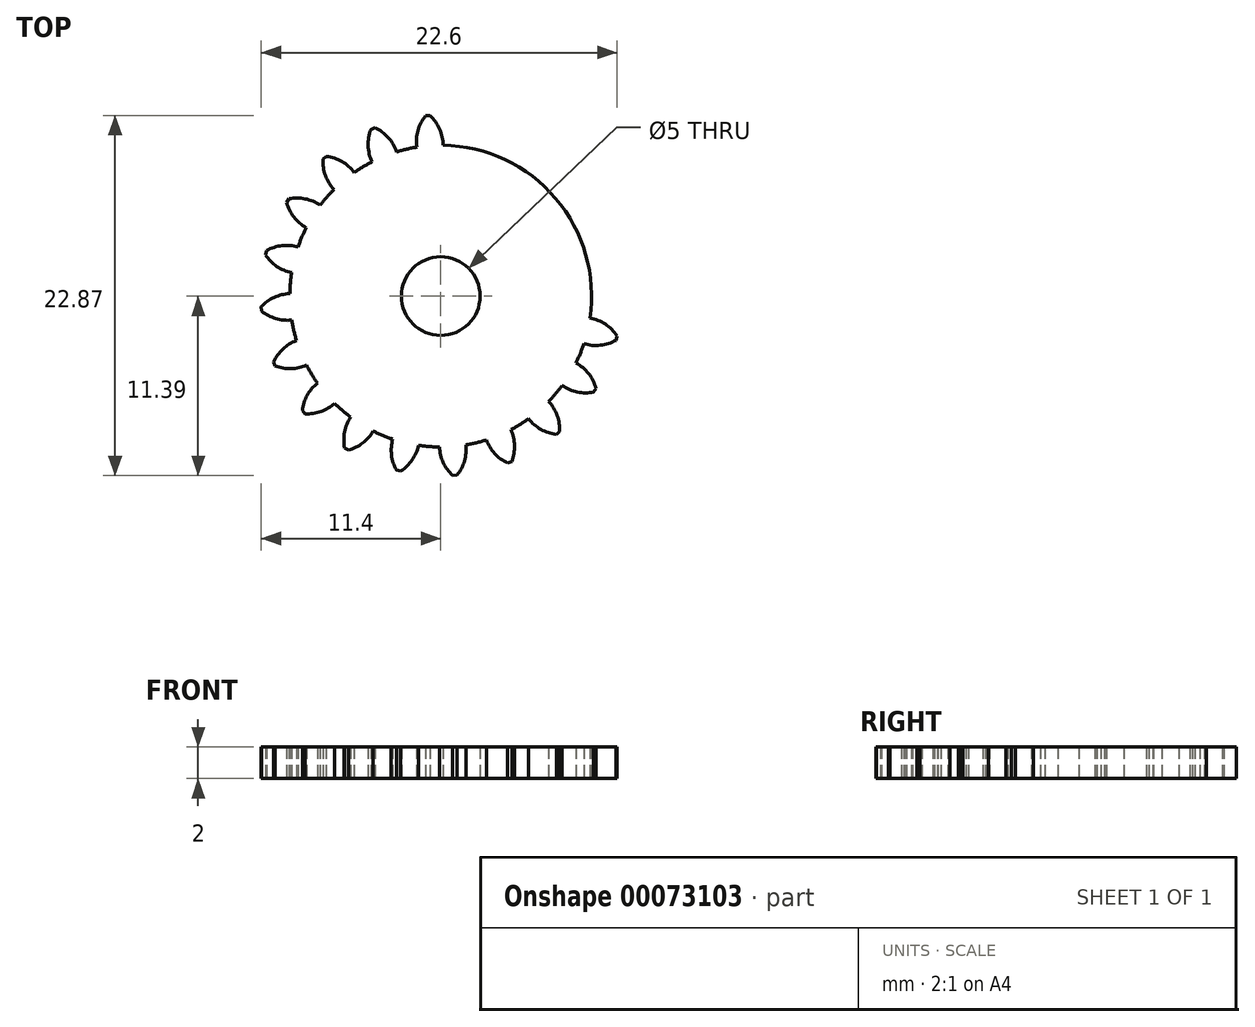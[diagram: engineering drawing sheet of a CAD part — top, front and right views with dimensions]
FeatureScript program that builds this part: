
annotation { "Feature Type Name" : "Feature", "Feature Type Description" : "" }
export const myFeature = defineFeature(function(context is Context, id is Id, definition is map)
    precondition{}
    {
        {
            assignVariable(context, id + "F0", {"name" : "GearDepth", "anyValue" : 2});
        }
        {
            var Q0;
            Q0=qCreatedBy(makeId("Top.planeOp"),FACE);
            var sketch = newSketch(context, id + "F1", { "sketchPlane" : qUnion([Q0])});
            skCircle(sketch, "E0", {"center": v(0, 0) * mm, "radius": 9.58 * mm});
            skCircle(sketch, "E1", {"center": v(0, 0) * mm, "radius": 10.54 * mm, "construction": true});
            skCircle(sketch, "E2", {"center": v(0, 0) * mm, "radius": 11.5 * mm, "construction": true});
            skLineSegment(sketch, "E3", {"start": v(0, 0) * mm, "end": v(0, 17.6) * mm, "construction": true});
            skLineSegment(sketch, "E4", {"start": v(0, 0) * mm, "end": v(-1.29, 18) * mm, "construction": true});
            skLineSegment(sketch, "E5", {"start": v(0, 10.54) * mm, "end": v(-10.54, 10.54) * mm, "construction": true});
            skLineSegment(sketch, "E6", {"start": v(0, 10.54) * mm, "end": v(-10.15, 6.44) * mm, "construction": true});
            skCircle(sketch, "E7", {"center": v(0, 10.54) * mm, "radius": 2.64 * mm, "construction": true});
            skCircle(sketch, "E8", {"center": v(-2.44, 9.55) * mm, "radius": 2.64 * mm, "construction": true});
            skArc(sketch, "E9", {"start": v(-4.89, 10.54) * mm, "mid": v(-4.92, 10.46) * mm, "end": v(-4.95, 10.38) * mm});
            skArc(sketch, "E10.trimOffspring", {"start": v(0.16, 9.58) * mm, "mid": v(-0.07, 10.62) * mm, "end": v(-0.68, 11.48) * mm});
            skArc(sketch, "E11.MirrorCS", {"start": v(-1.52, 9.46) * mm, "mid": v(-1.45, 10.52) * mm, "end": v(-0.96, 11.46) * mm});
            skLineSegment(sketch, "E12", {"start": v(-0.96, 11.46) * mm, "end": v(-0.68, 11.48) * mm});
            skArc(sketch, "E13.1.0", {"start": v(-2.8, 9.15) * mm, "mid": v(-3.33, 10.07) * mm, "end": v(-4.18, 10.7) * mm});
            skLineSegment(sketch, "E13.1.1", {"start": v(-4.44, 10.6) * mm, "end": v(-4.18, 10.7) * mm});
            skArc(sketch, "E13.1.2", {"start": v(-4.35, 8.52) * mm, "mid": v(-4.6, 9.55) * mm, "end": v(-4.44, 10.6) * mm});
            skArc(sketch, "E13.2.0", {"start": v(-5.47, 7.83) * mm, "mid": v(-6.26, 8.54) * mm, "end": v(-7.27, 8.87) * mm});
            skLineSegment(sketch, "E13.2.1", {"start": v(-7.48, 8.7) * mm, "end": v(-7.27, 8.87) * mm});
            skArc(sketch, "E13.2.2", {"start": v(-6.76, 6.75) * mm, "mid": v(-7.32, 7.65) * mm, "end": v(-7.48, 8.7) * mm});
            skArc(sketch, "E13.3.0", {"start": v(-7.6, 5.75) * mm, "mid": v(-8.58, 6.17) * mm, "end": v(-9.64, 6.18) * mm});
            skLineSegment(sketch, "E13.3.1", {"start": v(-9.78, 5.95) * mm, "end": v(-9.64, 6.18) * mm});
            skArc(sketch, "E13.3.2", {"start": v(-8.5, 4.32) * mm, "mid": v(-9.3, 5) * mm, "end": v(-9.78, 5.95) * mm});
            skArc(sketch, "E13.4.0", {"start": v(-9, 3.1) * mm, "mid": v(-10.05, 3.21) * mm, "end": v(-11.06, 2.9) * mm});
            skLineSegment(sketch, "E13.4.1", {"start": v(-11.13, 2.62) * mm, "end": v(-11.06, 2.9) * mm});
            skArc(sketch, "E13.4.2", {"start": v(-9.4, 1.47) * mm, "mid": v(-10.38, 1.87) * mm, "end": v(-11.13, 2.62) * mm});
            skArc(sketch, "E13.5.0", {"start": v(-9.5, 0.16) * mm, "mid": v(-10.53, -0.06) * mm, "end": v(-11.4, -0.68) * mm});
            skLineSegment(sketch, "E13.5.1", {"start": v(-11.38, -0.95) * mm, "end": v(-11.4, -0.68) * mm});
            skArc(sketch, "E13.5.2", {"start": v(-9.38, -1.51) * mm, "mid": v(-10.44, -1.44) * mm, "end": v(-11.38, -0.95) * mm});
            skArc(sketch, "E13.6.0", {"start": v(-9.07, -2.8) * mm, "mid": v(-9.98, -3.32) * mm, "end": v(-10.61, -4.17) * mm});
            skLineSegment(sketch, "E13.6.1", {"start": v(-10.51, -4.43) * mm, "end": v(-10.61, -4.17) * mm});
            skArc(sketch, "E13.6.2", {"start": v(-8.44, -4.35) * mm, "mid": v(-9.46, -4.6) * mm, "end": v(-10.51, -4.43) * mm});
            skArc(sketch, "E13.7.0", {"start": v(-7.75, -5.47) * mm, "mid": v(-8.45, -6.26) * mm, "end": v(-8.79, -7.26) * mm});
            skLineSegment(sketch, "E13.7.1", {"start": v(-8.61, -7.47) * mm, "end": v(-8.79, -7.26) * mm});
            skArc(sketch, "E13.7.2", {"start": v(-6.67, -6.75) * mm, "mid": v(-7.56, -7.31) * mm, "end": v(-8.61, -7.47) * mm});
            skArc(sketch, "E13.8.0", {"start": v(-5.66, -7.6) * mm, "mid": v(-6.1, -8.57) * mm, "end": v(-6.1, -9.63) * mm});
            skLineSegment(sketch, "E13.8.1", {"start": v(-5.86, -9.78) * mm, "end": v(-6.1, -9.63) * mm});
            skArc(sketch, "E13.8.2", {"start": v(-4.24, -8.49) * mm, "mid": v(-4.92, -9.3) * mm, "end": v(-5.86, -9.78) * mm});
            skArc(sketch, "E13.9.0", {"start": v(-3.02, -9) * mm, "mid": v(-3.13, -10.04) * mm, "end": v(-2.81, -11.05) * mm});
            skLineSegment(sketch, "E13.9.1", {"start": v(-2.54, -11.12) * mm, "end": v(-2.81, -11.05) * mm});
            skArc(sketch, "E13.9.2", {"start": v(-1.4, -9.4) * mm, "mid": v(-1.79, -10.38) * mm, "end": v(-2.54, -11.12) * mm});
            skArc(sketch, "E13.10.0", {"start": v(-0.08, -9.5) * mm, "mid": v(0.14, -10.53) * mm, "end": v(0.76, -11.4) * mm});
            skLineSegment(sketch, "E13.10.1", {"start": v(1.04, -11.37) * mm, "end": v(0.76, -11.4) * mm});
            skArc(sketch, "E13.10.2", {"start": v(1.6, -9.37) * mm, "mid": v(1.52, -10.43) * mm, "end": v(1.04, -11.37) * mm});
            skArc(sketch, "E13.11.0", {"start": v(2.87, -9.06) * mm, "mid": v(3.4, -9.98) * mm, "end": v(4.26, -10.6) * mm});
            skLineSegment(sketch, "E13.11.1", {"start": v(4.51, -10.5) * mm, "end": v(4.26, -10.6) * mm});
            skArc(sketch, "E13.11.2", {"start": v(4.43, -8.43) * mm, "mid": v(4.69, -9.46) * mm, "end": v(4.51, -10.5) * mm});
            skArc(sketch, "E13.12.0", {"start": v(5.55, -7.74) * mm, "mid": v(6.34, -8.45) * mm, "end": v(7.34, -8.78) * mm});
            skLineSegment(sketch, "E13.12.1", {"start": v(7.56, -8.6) * mm, "end": v(7.34, -8.78) * mm});
            skArc(sketch, "E13.12.2", {"start": v(6.83, -6.66) * mm, "mid": v(7.4, -7.56) * mm, "end": v(7.56, -8.6) * mm});
            skArc(sketch, "E13.13.0", {"start": v(7.69, -5.66) * mm, "mid": v(8.65, -6.09) * mm, "end": v(9.71, -6.1) * mm});
            skLineSegment(sketch, "E13.13.1", {"start": v(9.86, -5.86) * mm, "end": v(9.71, -6.1) * mm});
            skArc(sketch, "E13.13.2", {"start": v(8.57, -4.23) * mm, "mid": v(9.38, -4.91) * mm, "end": v(9.86, -5.86) * mm});
            skArc(sketch, "E13.14.0", {"start": v(9.07, -3.01) * mm, "mid": v(10.13, -3.12) * mm, "end": v(11.14, -2.8) * mm});
            skLineSegment(sketch, "E13.14.1", {"start": v(11.2, -2.53) * mm, "end": v(11.14, -2.8) * mm});
            skArc(sketch, "E13.14.2", {"start": v(9.48, -1.39) * mm, "mid": v(10.46, -1.78) * mm, "end": v(11.2, -2.53) * mm});
            skArc(sketch, "E13.15.0", {"start": v(9.58, -0.07) * mm, "mid": v(10.61, 0.15) * mm, "end": v(11.47, 0.76) * mm});
            skLineSegment(sketch, "E13.15.1", {"start": v(11.45, 1.04) * mm, "end": v(11.47, 0.76) * mm});
            skArc(sketch, "E13.15.2", {"start": v(9.46, 1.6) * mm, "mid": v(10.51, 1.53) * mm, "end": v(11.45, 1.04) * mm});
            skArc(sketch, "E13.16.0", {"start": v(9.15, 2.88) * mm, "mid": v(10.06, 3.41) * mm, "end": v(10.7, 4.26) * mm});
            skLineSegment(sketch, "E13.16.1", {"start": v(10.59, 4.52) * mm, "end": v(10.7, 4.26) * mm});
            skArc(sketch, "E13.16.2", {"start": v(8.51, 4.44) * mm, "mid": v(9.54, 4.7) * mm, "end": v(10.59, 4.52) * mm});
            skArc(sketch, "E13.17.0", {"start": v(7.82, 5.56) * mm, "mid": v(8.53, 6.34) * mm, "end": v(8.87, 7.35) * mm});
            skLineSegment(sketch, "E13.17.1", {"start": v(8.69, 7.56) * mm, "end": v(8.87, 7.35) * mm});
            skArc(sketch, "E13.17.2", {"start": v(6.74, 6.84) * mm, "mid": v(7.64, 7.4) * mm, "end": v(8.69, 7.56) * mm});
            skArc(sketch, "E13.18.0", {"start": v(5.74, 7.7) * mm, "mid": v(6.17, 8.66) * mm, "end": v(6.18, 9.72) * mm});
            skLineSegment(sketch, "E13.18.1", {"start": v(5.94, 9.87) * mm, "end": v(6.18, 9.72) * mm});
            skArc(sketch, "E13.18.2", {"start": v(4.31, 8.58) * mm, "mid": v(5, 9.4) * mm, "end": v(5.94, 9.87) * mm});
            skArc(sketch, "E13.19.0", {"start": v(3.1, 9.08) * mm, "mid": v(3.2, 10.13) * mm, "end": v(2.89, 11.14) * mm});
            skLineSegment(sketch, "E13.19.1", {"start": v(2.62, 11.2) * mm, "end": v(2.89, 11.14) * mm});
            skArc(sketch, "E13.19.2", {"start": v(1.47, 9.48) * mm, "mid": v(1.86, 10.46) * mm, "end": v(2.62, 11.2) * mm});
            skPoint(sketch, "E13.center", {"position": v(0.04, 0.04) * mm});
            skCircle(sketch, "E14", {"center": v(0, 0) * mm, "radius": 2.5 * mm});
            skSolve(sketch);
        }
        {
            var Q0;
            {var subQ0=sQuery(id+"F1.wireOp",EDGE,"E10.trimOffspring");Q0=makeQuery(id+"F1.imprint","IMPRINT",FACE,{"disambiguationData":[TD([[makeQuery(id+"F1.imprint","IMPRINT",EDGE,{"derivedFrom":subQ0}),1.0]])]});}
            var Q1;
            {var subQ0=sQuery(id+"F1.wireOp",EDGE,"E0");var subQ1=makeQuery(id+"F1.imprint","INTERSECT",VERTEX,{"derivedFrom":[subQ0,sQuery(id+"F1.wireOp",EDGE,"E10.trimOffspring")]});Q1=makeQuery(id+"F1.imprint","IMPRINT",FACE,{"disambiguationData":[TD([[makeQuery(id+"F1.imprint","IMPRINT",EDGE,{"disambiguationData":[TD([[subQ1,-1.0]])],"derivedFrom":subQ0}),1.0]])]});}
            var Q2;
            {var subQ0=sQuery(id+"F1.wireOp",EDGE,"E13.1.0");Q2=makeQuery(id+"F1.imprint","IMPRINT",FACE,{"disambiguationData":[TD([[makeQuery(id+"F1.imprint","IMPRINT",EDGE,{"derivedFrom":subQ0}),1.0]])]});}
            var Q3;
            {var subQ0=sQuery(id+"F1.wireOp",EDGE,"E13.2.0");Q3=makeQuery(id+"F1.imprint","IMPRINT",FACE,{"disambiguationData":[TD([[makeQuery(id+"F1.imprint","IMPRINT",EDGE,{"derivedFrom":subQ0}),1.0]])]});}
            var Q4;
            {var subQ0=sQuery(id+"F1.wireOp",EDGE,"E13.3.0");Q4=makeQuery(id+"F1.imprint","IMPRINT",FACE,{"disambiguationData":[TD([[makeQuery(id+"F1.imprint","IMPRINT",EDGE,{"derivedFrom":subQ0}),1.0]])]});}
            var Q5;
            {var subQ0=sQuery(id+"F1.wireOp",EDGE,"E13.4.0");Q5=makeQuery(id+"F1.imprint","IMPRINT",FACE,{"disambiguationData":[TD([[makeQuery(id+"F1.imprint","IMPRINT",EDGE,{"derivedFrom":subQ0}),1.0]])]});}
            var Q6;
            {var subQ0=sQuery(id+"F1.wireOp",EDGE,"E13.5.0");Q6=makeQuery(id+"F1.imprint","IMPRINT",FACE,{"disambiguationData":[TD([[makeQuery(id+"F1.imprint","IMPRINT",EDGE,{"derivedFrom":subQ0}),1.0]])]});}
            var Q7;
            {var subQ0=sQuery(id+"F1.wireOp",EDGE,"E13.6.0");Q7=makeQuery(id+"F1.imprint","IMPRINT",FACE,{"disambiguationData":[TD([[makeQuery(id+"F1.imprint","IMPRINT",EDGE,{"derivedFrom":subQ0}),1.0]])]});}
            var Q8;
            {var subQ0=sQuery(id+"F1.wireOp",EDGE,"E13.7.0");Q8=makeQuery(id+"F1.imprint","IMPRINT",FACE,{"disambiguationData":[TD([[makeQuery(id+"F1.imprint","IMPRINT",EDGE,{"derivedFrom":subQ0}),1.0]])]});}
            var Q9;
            {var subQ0=sQuery(id+"F1.wireOp",EDGE,"E13.8.0");Q9=makeQuery(id+"F1.imprint","IMPRINT",FACE,{"disambiguationData":[TD([[makeQuery(id+"F1.imprint","IMPRINT",EDGE,{"derivedFrom":subQ0}),1.0]])]});}
            var Q10;
            {var subQ0=sQuery(id+"F1.wireOp",EDGE,"E13.9.0");Q10=makeQuery(id+"F1.imprint","IMPRINT",FACE,{"disambiguationData":[TD([[makeQuery(id+"F1.imprint","IMPRINT",EDGE,{"derivedFrom":subQ0}),1.0]])]});}
            var Q11;
            {var subQ0=sQuery(id+"F1.wireOp",EDGE,"E13.10.0");Q11=makeQuery(id+"F1.imprint","IMPRINT",FACE,{"disambiguationData":[TD([[makeQuery(id+"F1.imprint","IMPRINT",EDGE,{"derivedFrom":subQ0}),1.0]])]});}
            var Q12;
            {var subQ0=sQuery(id+"F1.wireOp",EDGE,"E13.11.0");Q12=makeQuery(id+"F1.imprint","IMPRINT",FACE,{"disambiguationData":[TD([[makeQuery(id+"F1.imprint","IMPRINT",EDGE,{"derivedFrom":subQ0}),1.0]])]});}
            var Q13;
            {var subQ0=sQuery(id+"F1.wireOp",EDGE,"E13.12.0");Q13=makeQuery(id+"F1.imprint","IMPRINT",FACE,{"disambiguationData":[TD([[makeQuery(id+"F1.imprint","IMPRINT",EDGE,{"derivedFrom":subQ0}),1.0]])]});}
            var Q14;
            {var subQ0=sQuery(id+"F1.wireOp",EDGE,"E13.13.0");Q14=makeQuery(id+"F1.imprint","IMPRINT",FACE,{"disambiguationData":[TD([[makeQuery(id+"F1.imprint","IMPRINT",EDGE,{"derivedFrom":subQ0}),1.0]])]});}
            var Q15;
            {var subQ0=sQuery(id+"F1.wireOp",EDGE,"E13.14.0");Q15=makeQuery(id+"F1.imprint","IMPRINT",FACE,{"disambiguationData":[TD([[makeQuery(id+"F1.imprint","IMPRINT",EDGE,{"derivedFrom":subQ0}),1.0]])]});}
            var Q16;
            {var subQ0=sQuery(id+"F1.wireOp",EDGE,"E13.15.0");Q16=makeQuery(id+"F1.imprint","IMPRINT",FACE,{"disambiguationData":[TD([[makeQuery(id+"F1.imprint","IMPRINT",EDGE,{"derivedFrom":subQ0}),1.0]])]});}
            var Q17;
            {var subQ0=sQuery(id+"F1.wireOp",EDGE,"E13.16.0");Q17=makeQuery(id+"F1.imprint","IMPRINT",FACE,{"disambiguationData":[TD([[makeQuery(id+"F1.imprint","IMPRINT",EDGE,{"derivedFrom":subQ0}),1.0]])]});}
            var Q18;
            {var subQ0=sQuery(id+"F1.wireOp",EDGE,"E13.17.0");Q18=makeQuery(id+"F1.imprint","IMPRINT",FACE,{"disambiguationData":[TD([[makeQuery(id+"F1.imprint","IMPRINT",EDGE,{"derivedFrom":subQ0}),1.0]])]});}
            var Q19;
            {var subQ0=sQuery(id+"F1.wireOp",EDGE,"E13.18.0");Q19=makeQuery(id+"F1.imprint","IMPRINT",FACE,{"disambiguationData":[TD([[makeQuery(id+"F1.imprint","IMPRINT",EDGE,{"derivedFrom":subQ0}),1.0]])]});}
            var Q20;
            {var subQ0=sQuery(id+"F1.wireOp",EDGE,"E13.19.0");Q20=makeQuery(id+"F1.imprint","IMPRINT",FACE,{"disambiguationData":[TD([[makeQuery(id+"F1.imprint","IMPRINT",EDGE,{"derivedFrom":subQ0}),1.0]])]});}
            var Q21;
            Q21=sQuery(id+"F1.wireOp",EDGE,"E0");
            var Q22;
            Q22=sQuery(id+"F1.wireOp",EDGE,"E10.trimOffspring");
            var Q23;
            Q23=sQuery(id+"F1.wireOp",EDGE,"E12");
            var Q24;
            Q24=sQuery(id+"F1.wireOp",EDGE,"E11.MirrorCS");
            extrude(context, id + "F2", {"entities" : qUnion([Q0, Q1, Q2, Q3, Q4, Q5, Q6, Q7, Q8, Q9, Q10, Q11, Q12, Q13, Q14, Q15, Q16, Q17, Q18, Q19, Q20]), "surfaceEntities" : qUnion([Q21, Q22, Q23, Q24]), "depth" : (getVariable(context, 'GearDepth')) * mm});
        }
    });
